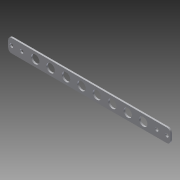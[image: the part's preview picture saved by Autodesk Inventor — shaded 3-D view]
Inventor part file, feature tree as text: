
AUTODESK INVENTOR PART (.ipt)
format: ipt  version: 2014 SP1 (Build 180222100, 222)  size: 125,440 bytes
history: native  units: in
note: dims shown in document units (in); Inventor stores cm internally (conversion verified against a paired STEP export)
features: other x3, sketch x1
ambient origin geometry x8: Origin, YZ Plane, XZ Plane, XY Plane, X Axis, Y Axis, Z Axis, Center Point
bodies: Solid1 (feature_tree)
feature tree (4):
  other  "V5 Shooter Frame Channel P7.ipt"
  other  "Solid1::V5 Shooter Frame Channel P7.ipt"
  sketch  "Sketch1"  dims[d0=0.3937in]
  other  "TaggingFeature1"
